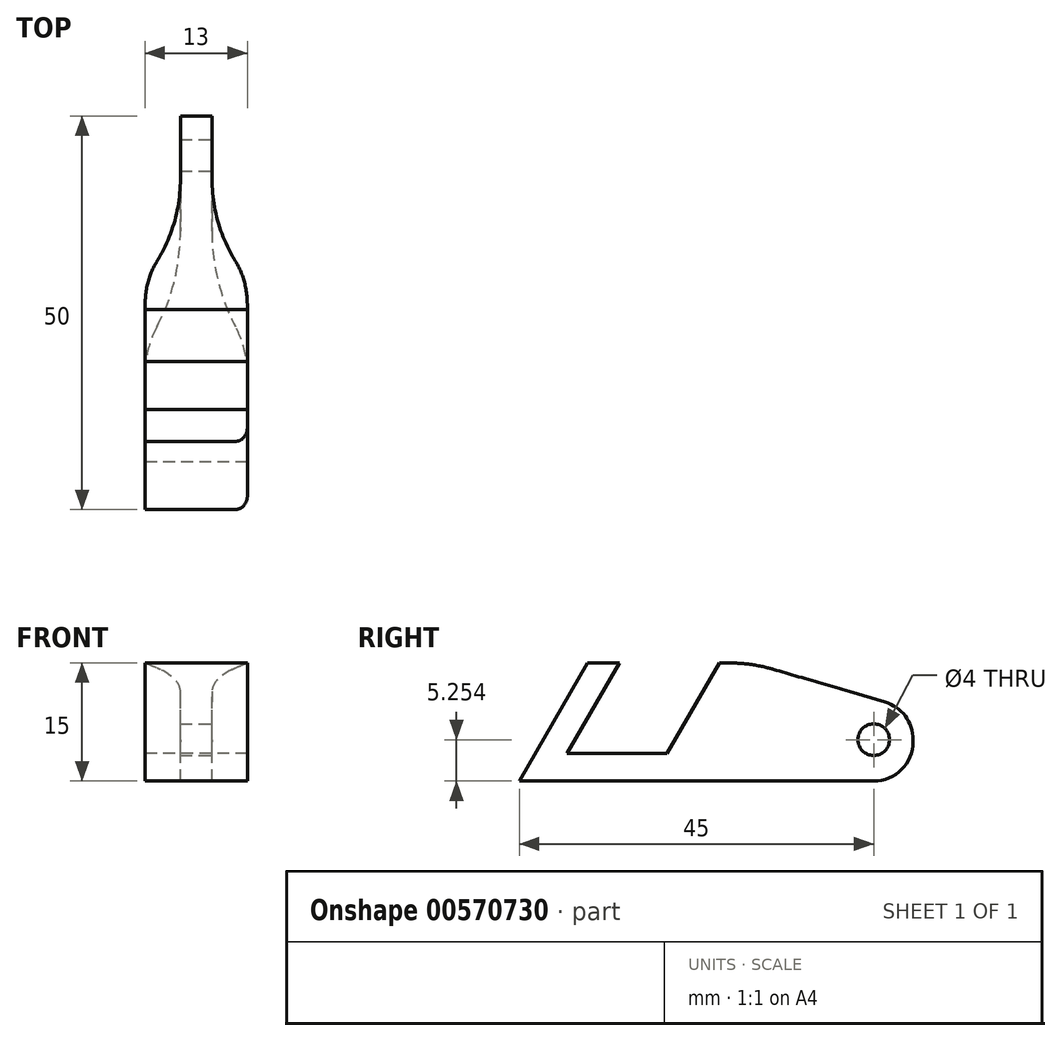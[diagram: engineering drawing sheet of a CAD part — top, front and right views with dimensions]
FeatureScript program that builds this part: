
annotation { "Feature Type Name" : "Feature", "Feature Type Description" : "" }
export const myFeature = defineFeature(function(context is Context, id is Id, definition is map)
    precondition{}
    {
        {
            var Q0;
            Q0=qCreatedBy(makeId("Top.planeOp"),FACE);
            var sketch = newSketch(context, id + "F0", { "sketchPlane" : qUnion([Q0])});
            skLineSegment(sketch, "E0.bottom", {"start": v(-6.5, -25) * mm, "end": v(6.5, -25) * mm});
            skLineSegment(sketch, "E0.top", {"start": v(-2, 25) * mm, "end": v(2, 25) * mm});
            skLineSegment(sketch, "E0.left", {"start": v(-6.5, -25) * mm, "end": v(-6.5, 12) * mm});
            skLineSegment(sketch, "E0.right", {"start": v(6.5, -25) * mm, "end": v(6.5, 12) * mm});
            skPoint(sketch, "E0.middle", {"position": v(0, 0) * mm});
            skLineSegment(sketch, "E1", {"start": v(0, 25) * mm, "end": v(0, 0) * mm, "construction": true});
            skLineSegment(sketch, "E2.left", {"start": v(-2, 25) * mm, "end": v(-2, 12) * mm});
            skLineSegment(sketch, "E2.right", {"start": v(2, 25) * mm, "end": v(2, 12) * mm});
            skLineSegment(sketch, "E3", {"start": v(-8.37, 12) * mm, "end": v(12.64, 12) * mm, "construction": true});
            skLineSegment(sketch, "E4", {"start": v(-2, 12) * mm, "end": v(-6.5, 12) * mm});
            skLineSegment(sketch, "E5", {"start": v(2, 12) * mm, "end": v(6.5, 12) * mm});
            skPoint(sketch, "E6.orphan", {"position": v(-6.5, 25) * mm});
            skPoint(sketch, "E7.orphan", {"position": v(6.5, 25) * mm});
            skSolve(sketch);
        }
        {
            var Q0;
            Q0=makeQuery(id+"F0.imprint","IMPRINT",FACE,{"disambiguationData":[TD([[makeQuery(id+"F0.imprint","IMPRINT",EDGE,{"derivedFrom":sQuery(id+"F0.wireOp",EDGE,"E0.bottom")}),1.0]])]});
            extrude(context, id + "F1", {"entities" : qUnion([Q0]), "depth" : 15 * mm, "offsetDistance" : 25 * mm});
        }
        {
            var Q0;
            Q0=makeQuery(id+"F1.opExtrude","SWEPT_FACE",FACE,{"disambiguationData":[OSD([sQuery(id+"F0.wireOp",EDGE,"E0.left")])]});
            var sketch = newSketch(context, id + "F2", { "sketchPlane" : qUnion([Q0])});
            skLineSegment(sketch, "E8", {"start": v(18.94, 3.5) * mm, "end": v(2.2, 3.5) * mm});
            skLineSegment(sketch, "E9", {"start": v(25, 0) * mm, "end": v(16.34, 15) * mm});
            skLineSegment(sketch, "E10", {"start": v(12.3, 15) * mm, "end": v(18.94, 3.5) * mm});
            skLineSegment(sketch, "E11", {"start": v(12.3, 15) * mm, "end": v(16.34, 15) * mm});
            skLineSegment(sketch, "E12", {"start": v(-0.4, 15) * mm, "end": v(6.24, 3.5) * mm});
            skLineSegment(sketch, "E13", {"start": v(-4.44, 15) * mm, "end": v(2.2, 3.5) * mm});
            skPoint(sketch, "E14.orphan", {"position": v(0, 3.5) * mm});
            skLineSegment(sketch, "E15", {"start": v(-4.44, 15) * mm, "end": v(-0.4, 15) * mm});
            skLineSegment(sketch, "E16", {"start": v(2.2, 3.5) * mm, "end": v(4.22, 0) * mm});
            skSolve(sketch);
        }
        {
            var Q0;
            {var subQ0=sQuery(id+"F2.wireOp",EDGE,"E10");Q0=makeQuery(id+"F2.imprint","IMPRINT",FACE,{"disambiguationData":[TD([[makeQuery(id+"F2.imprint","IMPRINT",EDGE,{"derivedFrom":subQ0}),-1.0]])]});}
            var Q1;
            {var subQ0=sQuery(id+"F2.wireOp",EDGE,"E9");Q1=makeQuery(id+"F2.imprint","IMPRINT",FACE,{"disambiguationData":[TD([[makeQuery(id+"F2.imprint","IMPRINT",EDGE,{"derivedFrom":subQ0}),-1.0]])]});}
            extrude(context, id + "F3", {"entities" : qUnion([Q0, Q1]), "operationType" : NewBodyOperationType.REMOVE, "oppositeDirection" : true, "depth" : 25 * mm, "offsetDistance" : 25 * mm});
        }
        {
            var Q0;
            {var subQ4=sQuery(id+"F2.wireOp",EDGE,"E13");Q0=makeQuery(id+"F2.imprint","IMPRINT",FACE,{"disambiguationData":[TD([[makeQuery(id+"F2.imprint","IMPRINT",EDGE,{"derivedFrom":subQ4}),-1.0]])]});}
            extrude(context, id + "F4", {"entities" : qUnion([Q0]), "operationType" : NewBodyOperationType.REMOVE, "oppositeDirection" : true, "depth" : 4.5 * mm, "offsetDistance" : 25 * mm});
        }
        {
            var Q0;
            Q0=makeQuery(id+"F1.opExtrude","SWEPT_FACE",FACE,{"disambiguationData":[OSD([sQuery(id+"F0.wireOp",EDGE,"E0.right")])]});
            var sketch = newSketch(context, id + "F5", { "sketchPlane" : qUnion([Q0])});
            skLineSegment(sketch, "E17", {"start": v(4.44, 15) * mm, "end": v(-4.22, 0) * mm});
            skSolve(sketch);
        }
        {
            var Q0;
            {var subQ0=sQuery(id+"F5.wireOp",EDGE,"E17");Q0=makeQuery(id+"F5.imprint","IMPRINT",FACE,{"disambiguationData":[TD([[makeQuery(id+"F5.imprint","IMPRINT",EDGE,{"derivedFrom":subQ0}),1.0]])]});}
            extrude(context, id + "F6", {"entities" : qUnion([Q0]), "operationType" : NewBodyOperationType.REMOVE, "oppositeDirection" : true, "depth" : 4.5 * mm, "offsetDistance" : 25 * mm});
        }
        {
            var Q0;
            Q0=makeQuery(id+"F6.boolean.opBoolean","COPY",EDGE,{"derivedFrom":makeQuery(id+"F6.opExtrude","CAP_EDGE",EDGE,{"disambiguationData":[OSD([sQuery(id+"F5.wireOp",EDGE,"E17")])],"isStart":false})});
            var Q1;
            Q1=makeQuery(id+"F4.boolean.opBoolean","COPY",EDGE,{"derivedFrom":makeQuery(id+"F4.opExtrude","CAP_EDGE",EDGE,{"disambiguationData":[OSD([sQuery(id+"F2.wireOp",EDGE,"E13"),sQuery(id+"F2.wireOp",EDGE,"E16")])],"isStart":false})});
            fillet(context, id + "F7", {"entities" : qUnion([Q0, Q1]), "radius" : 20 * mm, "tangentPropagation" : true, "allowEdgeOverflow" : false});
        }
        {
            var Q0;
            Q0=makeQuery(id+"F1.opExtrude","CAP_EDGE",EDGE,{"disambiguationData":[OSD([sQuery(id+"F0.wireOp",EDGE,"E0.top")])],"isStart":false});
            chamfer(context, id + "F8", {"entities" : qUnion([Q0]), "chamferType" : ChamferType.TWO_OFFSETS, "width1" : 6 * mm, "oppositeDirection" : false, "width2" : 20.5 * mm, "tangentPropagation" : true});
        }
        {
            var Q0;
            Q0=makeQuery(id+"F3.boolean.opBoolean","COPY",EDGE,{"derivedFrom":makeQuery(id+"F3.opExtrude","CAP_EDGE",EDGE,{"disambiguationData":[OSD([sQuery(id+"F2.wireOp",EDGE,"E9")])],"isStart":true})});
            var Q1;
            Q1=makeQuery(id+"F3.boolean.opBoolean","INTERSECT",EDGE,{"derivedFrom":[makeQuery(id+"F1.opExtrude","SWEPT_FACE",FACE,{"disambiguationData":[OSD([sQuery(id+"F0.wireOp",EDGE,"E0.right")])]}),makeQuery(id+"F3.opExtrude","SWEPT_FACE",FACE,{"disambiguationData":[OSD([sQuery(id+"F2.wireOp",EDGE,"E9")])]})]});
            fillet(context, id + "F9", {"entities" : qUnion([Q0, Q1]), "radius" : 1.5 * mm, "tangentPropagation" : true, "allowEdgeOverflow" : false});
        }
        {
            var Q0;
            Q0=makeQuery(id+"F7.opFillet","BLEND_EDGE",EDGE,{"blendedFrom":[makeQuery(id+"F4.boolean.opBoolean","COPY",EDGE,{"derivedFrom":makeQuery(id+"F4.opExtrude","CAP_EDGE",EDGE,{"disambiguationData":[OSD([sQuery(id+"F2.wireOp",EDGE,"E13"),sQuery(id+"F2.wireOp",EDGE,"E16")])],"isStart":false})}),makeQuery(id+"F1.opExtrude","SWEPT_FACE",FACE,{"disambiguationData":[OSD([sQuery(id+"F0.wireOp",EDGE,"E0.left")])]})],"blendedInto":[makeQuery(id+"F1.opExtrude","SWEPT_FACE",FACE,{"disambiguationData":[OSD([sQuery(id+"F0.wireOp",EDGE,"E0.left")])]})]});
            var Q1;
            Q1=makeQuery(id+"F7.opFillet","BLEND_EDGE",EDGE,{"blendedFrom":[makeQuery(id+"F6.boolean.opBoolean","COPY",EDGE,{"derivedFrom":makeQuery(id+"F6.opExtrude","CAP_EDGE",EDGE,{"disambiguationData":[OSD([sQuery(id+"F5.wireOp",EDGE,"E17")])],"isStart":false})}),makeQuery(id+"F1.opExtrude","SWEPT_FACE",FACE,{"disambiguationData":[OSD([sQuery(id+"F0.wireOp",EDGE,"E0.right")])]})],"blendedInto":[makeQuery(id+"F1.opExtrude","SWEPT_FACE",FACE,{"disambiguationData":[OSD([sQuery(id+"F0.wireOp",EDGE,"E0.right")])]})]});
            fillet(context, id + "F10", {"entities" : qUnion([Q0, Q1]), "radius" : 10 * mm, "tangentPropagation" : true, "allowEdgeOverflow" : false});
        }
        {
            var Q0;
            {var subQ0=sQuery(id+"F0.wireOp",EDGE,"E2.left");var subQ1=sQuery(id+"F0.wireOp",EDGE,"E0.top");var subQ2=sQuery(id+"F0.wireOp",EDGE,"E0.right");var subQ3=sQuery(id+"F0.wireOp",EDGE,"E0.left");var subQ4=sQuery(id+"F0.wireOp",EDGE,"E2.right");var subQ5=sQuery(id+"F0.wireOp",EDGE,"E4");var subQ6=sQuery(id+"F0.wireOp",EDGE,"E5");Q0=makeQuery(id+"F8.opChamfer","BLEND_EDGE",EDGE,{"blendedFrom":[makeQuery(id+"F1.opExtrude","CAP_EDGE",EDGE,{"disambiguationData":[OSD([subQ1])],"isStart":false}),makeQuery(id+"F3.boolean.opBoolean","SPLIT",FACE,{"disambiguationData":[TD([makeQuery(id+"F1.opExtrude","SWEPT_FACE",FACE,{"disambiguationData":[OSD([subQ1])]})])],"derivedFrom":makeQuery(id+"F1.opExtrude","CAP_FACE",FACE,{"disambiguationData":[OSD([sQuery(id+"F0.wireOp",EDGE,"E0.bottom"),subQ3,subQ2,subQ1,subQ0,subQ4,subQ5,subQ6])],"isStart":false})})],"blendedInto":[makeQuery(id+"F3.boolean.opBoolean","SPLIT",FACE,{"disambiguationData":[TD([makeQuery(id+"F1.opExtrude","SWEPT_FACE",FACE,{"disambiguationData":[OSD([subQ1])]})])],"derivedFrom":makeQuery(id+"F1.opExtrude","CAP_FACE",FACE,{"disambiguationData":[OSD([sQuery(id+"F0.wireOp",EDGE,"E0.bottom"),subQ3,subQ2,subQ1,subQ0,subQ4,subQ5,subQ6])],"isStart":false})})]});}
            fillet(context, id + "F11", {"entities" : qUnion([Q0]), "radius" : 20 * mm, "tangentPropagation" : true, "allowEdgeOverflow" : false});
        }
        {
            var Q0;
            {var subQ0=sQuery(id+"F0.wireOp",EDGE,"E0.top");Q0=makeQuery(id+"F8.opChamfer","BLEND_EDGE",EDGE,{"blendedFrom":[makeQuery(id+"F1.opExtrude","CAP_EDGE",EDGE,{"disambiguationData":[OSD([subQ0])],"isStart":false}),makeQuery(id+"F1.opExtrude","SWEPT_FACE",FACE,{"disambiguationData":[OSD([subQ0])]})],"blendedInto":[makeQuery(id+"F1.opExtrude","SWEPT_FACE",FACE,{"disambiguationData":[OSD([subQ0])]})]});}
            var Q1;
            Q1=makeQuery(id+"F1.opExtrude","CAP_EDGE",EDGE,{"disambiguationData":[OSD([sQuery(id+"F0.wireOp",EDGE,"E0.top")])],"isStart":true});
            fillet(context, id + "F12", {"entities" : qUnion([Q0, Q1]), "radius" : 5 * mm, "tangentPropagation" : true, "allowEdgeOverflow" : false});
        }
        {
            var Q0;
            Q0=makeQuery(id+"F6.boolean.opBoolean","MERGE",FACE,{"derivedFrom":[makeQuery(id+"F1.opExtrude","SWEPT_FACE",FACE,{"disambiguationData":[OSD([sQuery(id+"F0.wireOp",EDGE,"E2.right")])]}),makeQuery(id+"F6.opExtrude","CAP_FACE",FACE,{"disambiguationData":[OSD([sQuery(id+"F0.wireOp",EDGE,"E0.right"),sQuery(id+"F0.wireOp",EDGE,"E5"),sQuery(id+"F5.wireOp",EDGE,"E17")])],"isStart":false})]});
            var sketch = newSketch(context, id + "F13", { "sketchPlane" : qUnion([Q0])});
            skCircle(sketch, "E18", {"center": v(20, 5.25) * mm, "radius": 2 * mm});
            skSolve(sketch);
        }
        {
            var Q0;
            Q0=makeQuery(id+"F13.imprint","IMPRINT",FACE,{"disambiguationData":[TD([[makeQuery(id+"F13.imprint","IMPRINT",EDGE,{"derivedFrom":sQuery(id+"F13.wireOp",EDGE,"E18")}),1.0]])]});
            var Q1;
            Q1=sQuery(id+"F13.wireOp",EDGE,"E18");
            extrude(context, id + "F14", {"entities" : qUnion([Q0]), "operationType" : NewBodyOperationType.REMOVE, "surfaceEntities" : qUnion([Q1]), "oppositeDirection" : true, "depth" : 25 * mm, "offsetDistance" : 25 * mm});
        }
    });
